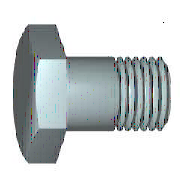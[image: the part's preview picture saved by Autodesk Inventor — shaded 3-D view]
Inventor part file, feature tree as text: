
AUTODESK INVENTOR PART (.ipt)
format: ipt  version: 2024 (Build 280153000, 153)  size: 199,168 bytes
history: native  units: mm (DEFAULTED — no unit token found)
features: other x4, plane x3, sketch x2, chamfer x1, fillet x1
ambient origin geometry x6: Origin, XY Plane, X Axis, Y Axis, Z Axis, Center Point
bodies: Solid1 (feature_tree)
feature tree (11):
  plane  "WorkPlane1"
  sketch  "Sketch1"  dims[d0=30.0mm]
  other  "WorkPoint1"
  chamfer  "Chamfer1"  Distance=15.0mm
  fillet  "Fillet1"  Radius=17.321016mm
  other  "MSC_A1"
  other  "MSC_PF1"
  other  "MSC_PT1"
  plane  "WorkPlane2"
  plane  "WorkPlane3"
  sketch  "Sketch2"  dims[d1=13.0mm d2=15.0mm d4=17.321016mm d6=5.3mm d7=0.0mm d8=15.0mm d10=0.0mm d12=30.0deg d14=360.0deg d15=0.0mm d17=10.0mm d18=4.0mm d19=80.0mm d20=80.0mm d21=360.0deg d22=0.625mm d23=0.625mm d24=0.4mm d25=0.1mm d26=0.0mm d27=60.0deg d28=6.5mm d29=0.0mm d30=0.0mm d32=0.0mm d33=0.0mm d34=0.0mm d37=0.0mm d38=0.0mm d39=45.0deg d40=0.0mm d41=0.0mm d42=0.0mm]
